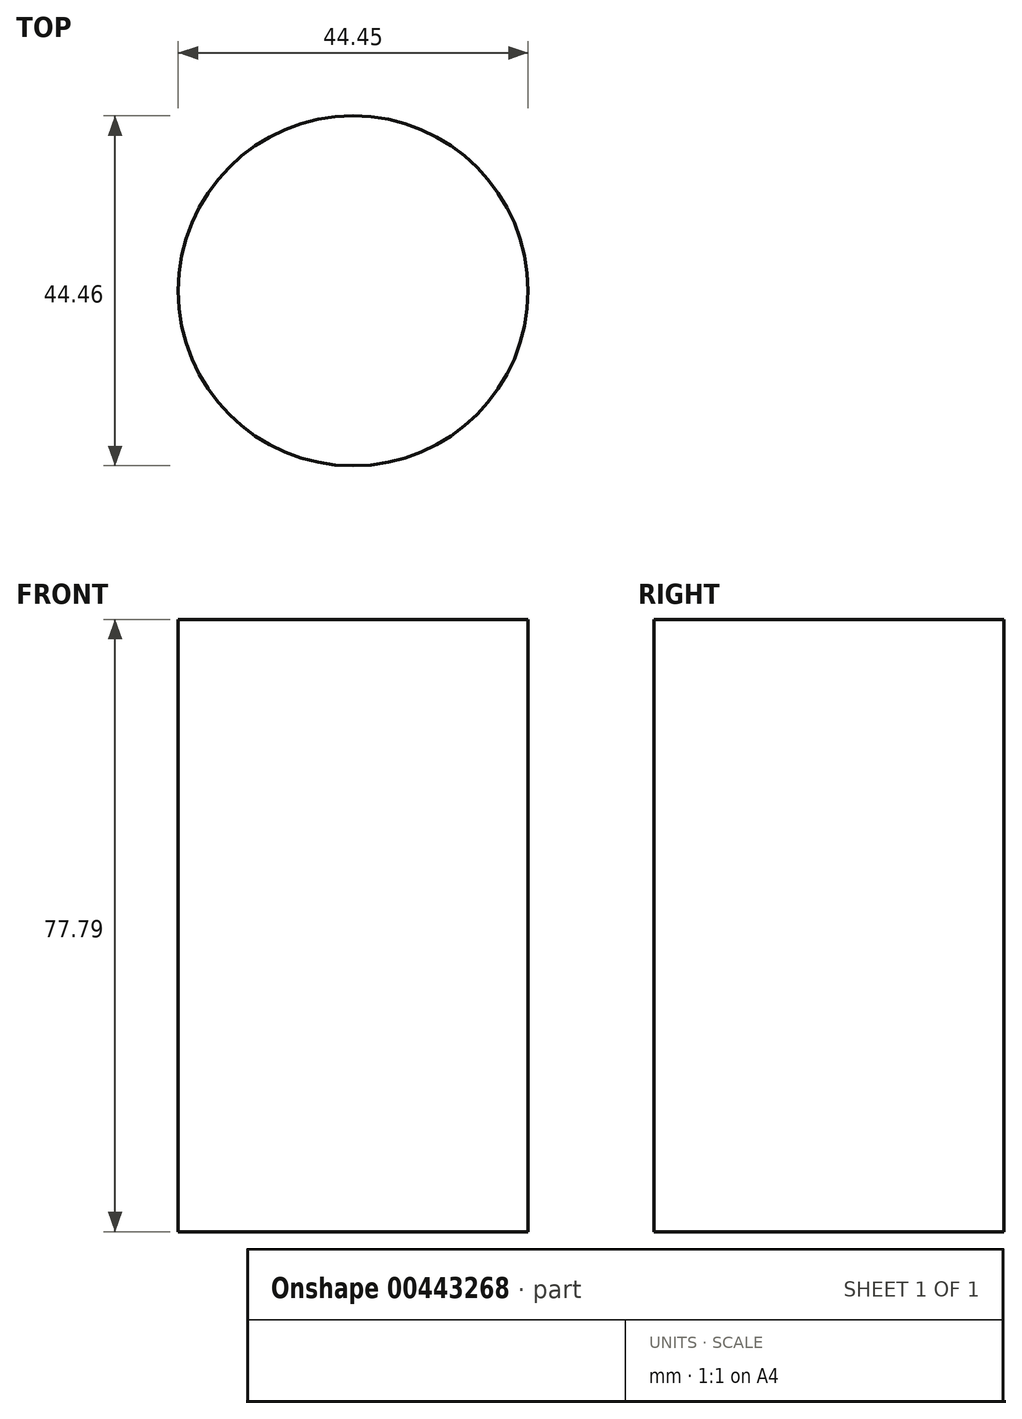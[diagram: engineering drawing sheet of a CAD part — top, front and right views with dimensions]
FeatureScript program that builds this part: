
annotation { "Feature Type Name" : "Feature", "Feature Type Description" : "" }
export const myFeature = defineFeature(function(context is Context, id is Id, definition is map)
    precondition{}
    {
        {
            var Q0;
            Q0=qCreatedBy(makeId("Top.planeOp"),FACE);
            var sketch = newSketch(context, id + "F0", { "sketchPlane" : qUnion([Q0])});
            skCircle(sketch, "E0", {"center": v(-1.69, 0) * mm, "radius": 22.23 * mm});
            skSolve(sketch);
        }
        {
            var Q0;
            Q0 = qSketchRegion(id + "F0", true);
            extrude(context, id + "F1", {"entities" : qUnion([Q0]), "depth" : 77.8 * mm});
        }
    });
